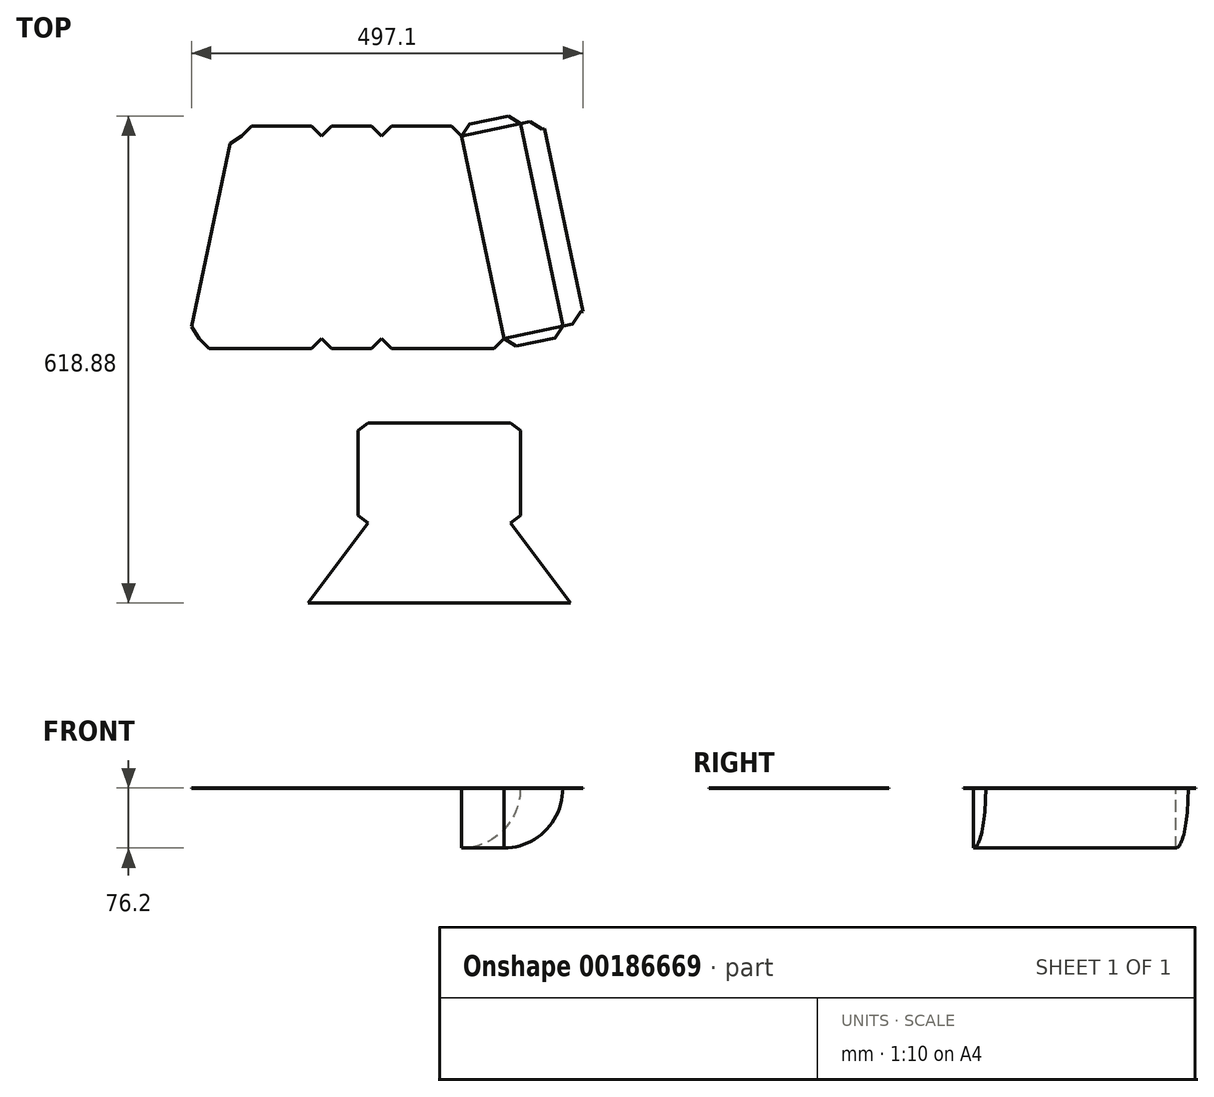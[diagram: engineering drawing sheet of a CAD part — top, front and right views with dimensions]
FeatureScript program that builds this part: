
annotation { "Feature Type Name" : "Feature", "Feature Type Description" : "" }
export const myFeature = defineFeature(function(context is Context, id is Id, definition is map)
    precondition{}
    {
        {
            assignVariable(context, id + "F0", {"name" : "Length", "anyValue" : 10.12});
        }
        {
            var Q0;
            Q0=qCreatedBy(makeId("Front.planeOp"),FACE);
            var sketch = newSketch(context, id + "F1", { "sketchPlane" : qUnion([Q0])});
            skLineSegment(sketch, "E0.bottom", {"start": v(-75.35, 24.33) * mm, "end": v(80.22, 24.33) * mm});
            skLineSegment(sketch, "E0.top", {"start": v(-75.35, -51.87) * mm, "end": v(80.22, -51.87) * mm});
            skLineSegment(sketch, "E0.left", {"start": v(-75.35, 24.33) * mm, "end": v(-75.35, -51.87) * mm});
            skLineSegment(sketch, "E0.right", {"start": v(80.22, 24.33) * mm, "end": v(80.22, -51.87) * mm});
            skSolve(sketch);
        }
        {
            var Q0;
            Q0=qCreatedBy(makeId("Front.planeOp"),FACE);
            cPlane(context, id + "F2", {"entities" : qUnion([Q0]), "cplaneType" : CPlaneType.OFFSET, "offset" : (getVariable(context, 'Length')) * mm, "oppositeDirection" : true, "width" : 152.4 * mm, "height" : 152.4 * mm});
        }
        {
            var Q0;
            Q0=qCreatedBy(id+"F2.planeOp",FACE);
            var sketch = newSketch(context, id + "F3", { "sketchPlane" : qUnion([Q0])});
            skLineSegment(sketch, "E1.bottom", {"start": v(-75.35, 24.33) * mm, "end": v(26.25, 24.33) * mm});
            skLineSegment(sketch, "E1.top", {"start": v(-75.35, -51.87) * mm, "end": v(26.25, -51.87) * mm});
            skLineSegment(sketch, "E1.left", {"start": v(-75.35, 24.33) * mm, "end": v(-75.35, -51.87) * mm});
            skLineSegment(sketch, "E1.right", {"start": v(26.25, 24.33) * mm, "end": v(26.25, -51.87) * mm});
            skSolve(sketch);
        }
        {
            var Q0;
            Q0=sQuery(id+"F3.wireOp",EDGE,"E1.bottom");
            var Q1;
            Q1=sQuery(id+"F1.wireOp",EDGE,"E0.bottom");
            cPlane(context, id + "F4", {"entities" : qUnion([Q0, Q1]), "cplaneType" : CPlaneType.LINE_ANGLE, "offset" : 25.4 * mm, "angle" : 0 * degree, "width" : 152.4 * mm, "height" : 152.4 * mm});
        }
        {
            var Q0;
            Q0=sQuery(id+"F3.wireOp",EDGE,"E1.top");
            var Q1;
            Q1=sQuery(id+"F1.wireOp",EDGE,"E0.top");
            cPlane(context, id + "F5", {"entities" : qUnion([Q0, Q1]), "cplaneType" : CPlaneType.LINE_ANGLE, "offset" : 25.4 * mm, "angle" : 0 * degree, "width" : 152.4 * mm, "height" : 152.4 * mm});
        }
        {
            var Q0;
            Q0=qCreatedBy(id+"F5.planeOp",FACE);
            var sketch = newSketch(context, id + "F6", { "sketchPlane" : qUnion([Q0])});
            skLineSegment(sketch, "E2", {"start": v(-75.35, -257.18) * mm, "end": v(-75.35, 0) * mm});
            skLineSegment(sketch, "E3", {"start": v(-75.35, 0) * mm, "end": v(80.22, 0) * mm});
            skLineSegment(sketch, "E4", {"start": v(80.22, 0) * mm, "end": v(26.25, -257.18) * mm});
            skLineSegment(sketch, "E5", {"start": v(26.25, -257.18) * mm, "end": v(-75.35, -257.18) * mm});
            skSolve(sketch);
        }
        {
            var Q0;
            Q0=qCreatedBy(id+"F4.planeOp",FACE);
            var sketch = newSketch(context, id + "F7", { "sketchPlane" : qUnion([Q0])});
            skLineSegment(sketch, "E6", {"start": v(-75.35, -257.18) * mm, "end": v(-75.35, 0) * mm});
            skLineSegment(sketch, "E7", {"start": v(-75.35, 0) * mm, "end": v(80.22, 0) * mm});
            skLineSegment(sketch, "E8", {"start": v(80.22, 0) * mm, "end": v(26.25, -257.18) * mm});
            skLineSegment(sketch, "E9", {"start": v(26.25, -257.18) * mm, "end": v(-75.35, -257.18) * mm});
            skSolve(sketch);
        }
        {
            var Q0;
            Q0=sQuery(id+"F7.wireOp",EDGE,"E8");
            var Q1;
            Q1=sQuery(id+"F6.wireOp",EDGE,"E4");
            cPlane(context, id + "F8", {"entities" : qUnion([Q0, Q1]), "cplaneType" : CPlaneType.LINE_ANGLE, "offset" : 25.4 * mm, "angle" : 0 * degree, "width" : 152.4 * mm, "height" : 152.4 * mm});
        }
        {
            var Q0;
            Q0=qCreatedBy(id+"F8.planeOp",FACE);
            var sketch = newSketch(context, id + "F9", { "sketchPlane" : qUnion([Q0])});
            skLineSegment(sketch, "E10", {"start": v(16.48, 24.33) * mm, "end": v(16.48, -51.87) * mm});
            skLineSegment(sketch, "E11", {"start": v(16.48, -51.87) * mm, "end": v(-246.3, -51.87) * mm});
            skLineSegment(sketch, "E12", {"start": v(-246.3, -51.87) * mm, "end": v(-246.3, 24.33) * mm});
            skLineSegment(sketch, "E13", {"start": v(-246.3, 24.33) * mm, "end": v(16.48, 24.33) * mm});
            skSolve(sketch);
        }
        {
            var Q0;
            Q0 = qSketchRegion(id + "F9", true);
            var Q1;
            Q1=sQuery(id+"F7.wireOp",EDGE,"E8");
            revolve(context, id + "F10", {"entities" : qUnion([Q0]), "axis" : qUnion([Q1]), "revolveType" : RevolveType.ONE_DIRECTION, "oppositeDirection" : true, "angle" : 90 * degree});
        }
        {
            var Q0;
            Q0=qCreatedBy(id+"F4.planeOp",FACE);
            var sketch = newSketch(context, id + "F11", { "sketchPlane" : qUnion([Q0])});
            skLineSegment(sketch, "E14", {"start": v(26.25, -257.18) * mm, "end": v(100.82, -272.83) * mm});
            skLineSegment(sketch, "E15", {"start": v(100.82, -272.83) * mm, "end": v(154.8, -15.65) * mm});
            skLineSegment(sketch, "E16", {"start": v(154.8, -15.65) * mm, "end": v(80.22, 0) * mm});
            skLineSegment(sketch, "E17", {"start": v(80.22, 0) * mm, "end": v(26.25, -257.18) * mm});
            skLineSegment(sketch, "E18", {"start": v(-75.35, -257.18) * mm, "end": v(-151.55, -257.18) * mm});
            skLineSegment(sketch, "E19", {"start": v(-151.55, -257.18) * mm, "end": v(-151.55, 0) * mm});
            skLineSegment(sketch, "E20", {"start": v(-151.55, 0) * mm, "end": v(-75.35, 0) * mm});
            skLineSegment(sketch, "E21", {"start": v(-75.35, 0) * mm, "end": v(-75.35, -257.18) * mm});
            skLineSegment(sketch, "E22", {"start": v(-151.55, 0) * mm, "end": v(-307.13, 0) * mm});
            skLineSegment(sketch, "E23", {"start": v(-307.13, 0) * mm, "end": v(-253.15, -257.18) * mm});
            skLineSegment(sketch, "E24", {"start": v(-253.15, -257.18) * mm, "end": v(-151.55, -257.18) * mm});
            skLineSegment(sketch, "E25", {"start": v(-75.35, -257.18) * mm, "end": v(26.25, -257.18) * mm});
            skLineSegment(sketch, "E26", {"start": v(-75.35, 0) * mm, "end": v(80.22, 0) * mm});
            skLineSegment(sketch, "E27", {"start": v(-307.13, 0) * mm, "end": v(-316.95, -15.04) * mm});
            skLineSegment(sketch, "E28", {"start": v(-316.95, -15.04) * mm, "end": v(-268.2, -247.35) * mm});
            skLineSegment(sketch, "E29", {"start": v(-268.2, -247.35) * mm, "end": v(-253.15, -257.18) * mm});
            skLineSegment(sketch, "E30", {"start": v(-280.14, -128.59) * mm, "end": v(-292.57, -131.2) * mm, "construction": true});
            skLineSegment(sketch, "E31", {"start": v(-151.55, -257.18) * mm, "end": v(-138.85, -269.88) * mm});
            skLineSegment(sketch, "E32", {"start": v(-138.85, -269.88) * mm, "end": v(-88.05, -269.88) * mm});
            skLineSegment(sketch, "E33", {"start": v(-88.05, -269.88) * mm, "end": v(-75.35, -257.18) * mm});
            skLineSegment(sketch, "E34", {"start": v(-75.35, -257.18) * mm, "end": v(-62.65, -269.88) * mm});
            skLineSegment(sketch, "E35", {"start": v(-62.65, -269.88) * mm, "end": v(13.55, -269.88) * mm});
            skLineSegment(sketch, "E36", {"start": v(13.55, -269.88) * mm, "end": v(26.25, -257.18) * mm});
            skLineSegment(sketch, "E37", {"start": v(-113.45, -257.18) * mm, "end": v(-113.45, -269.88) * mm, "construction": true});
            skLineSegment(sketch, "E38", {"start": v(-24.55, -257.18) * mm, "end": v(-24.55, -269.88) * mm, "construction": true});
            skLineSegment(sketch, "E39", {"start": v(-151.55, 0) * mm, "end": v(-138.85, 12.7) * mm});
            skLineSegment(sketch, "E40", {"start": v(-138.85, 12.7) * mm, "end": v(-88.05, 12.7) * mm});
            skLineSegment(sketch, "E41", {"start": v(-88.05, 12.7) * mm, "end": v(-75.35, 0) * mm});
            skLineSegment(sketch, "E42", {"start": v(-75.35, 0) * mm, "end": v(-62.65, 12.7) * mm});
            skLineSegment(sketch, "E43", {"start": v(-62.65, 12.7) * mm, "end": v(67.52, 12.7) * mm});
            skLineSegment(sketch, "E44", {"start": v(67.52, 12.7) * mm, "end": v(80.22, 0) * mm});
            skLineSegment(sketch, "E45", {"start": v(-151.55, 0) * mm, "end": v(-164.25, 12.7) * mm});
            skLineSegment(sketch, "E46", {"start": v(-164.25, 12.7) * mm, "end": v(-294.43, 12.7) * mm});
            skLineSegment(sketch, "E47", {"start": v(-294.43, 12.7) * mm, "end": v(-307.13, 0) * mm});
            skLineSegment(sketch, "E48", {"start": v(-253.15, -257.18) * mm, "end": v(-240.45, -269.88) * mm});
            skLineSegment(sketch, "E49", {"start": v(-240.45, -269.88) * mm, "end": v(-164.25, -269.88) * mm});
            skLineSegment(sketch, "E50", {"start": v(-164.25, -269.88) * mm, "end": v(-151.55, -257.18) * mm});
            skLineSegment(sketch, "E51", {"start": v(-202.35, -257.18) * mm, "end": v(-202.35, -269.88) * mm, "construction": true});
            skLineSegment(sketch, "E52", {"start": v(-229.34, 0) * mm, "end": v(-229.34, 12.7) * mm, "construction": true});
            skLineSegment(sketch, "E53", {"start": v(-113.45, 0) * mm, "end": v(-113.45, 12.7) * mm, "construction": true});
            skLineSegment(sketch, "E54", {"start": v(2.43, 0) * mm, "end": v(2.43, 12.7) * mm, "construction": true});
            skLineSegment(sketch, "E55", {"start": v(80.22, 0) * mm, "end": v(95.26, 9.82) * mm});
            skLineSegment(sketch, "E56", {"start": v(95.26, 9.82) * mm, "end": v(144.98, -0.61) * mm});
            skLineSegment(sketch, "E57", {"start": v(144.98, -0.61) * mm, "end": v(154.8, -15.65) * mm});
            skLineSegment(sketch, "E58", {"start": v(100.82, -272.83) * mm, "end": v(85.78, -282.65) * mm});
            skLineSegment(sketch, "E59", {"start": v(85.78, -282.65) * mm, "end": v(36.07, -272.21) * mm});
            skLineSegment(sketch, "E60", {"start": v(36.07, -272.21) * mm, "end": v(26.25, -257.18) * mm});
            skLineSegment(sketch, "E61", {"start": v(63.53, -265) * mm, "end": v(60.92, -277.43) * mm, "construction": true});
            skLineSegment(sketch, "E62", {"start": v(117.5, -7.83) * mm, "end": v(120.12, 4.6) * mm, "construction": true});
            skLineSegment(sketch, "E63", {"start": v(154.8, -15.65) * mm, "end": v(167.22, -18.26) * mm});
            skLineSegment(sketch, "E64", {"start": v(167.22, -18.26) * mm, "end": v(113.25, -275.44) * mm});
            skLineSegment(sketch, "E65", {"start": v(113.25, -275.44) * mm, "end": v(100.82, -272.83) * mm});
            skLineSegment(sketch, "E66", {"start": v(127.8, -144.24) * mm, "end": v(140.24, -146.85) * mm, "construction": true});
            skLineSegment(sketch, "E67", {"start": v(140.24, -146.85) * mm, "end": v(152.67, -149.46) * mm, "construction": true});
            skLineSegment(sketch, "E68", {"start": v(167.22, -18.26) * mm, "end": v(177.05, -33.3) * mm});
            skLineSegment(sketch, "E69", {"start": v(177.05, -33.3) * mm, "end": v(128.29, -265.61) * mm});
            skLineSegment(sketch, "E70", {"start": v(128.29, -265.61) * mm, "end": v(113.25, -275.44) * mm});
            skLineSegment(sketch, "E71", {"start": v(177.05, -33.3) * mm, "end": v(180.15, -33.95) * mm});
            skLineSegment(sketch, "E72", {"start": v(180.15, -33.95) * mm, "end": v(131.4, -266.27) * mm});
            skLineSegment(sketch, "E73", {"start": v(131.4, -266.27) * mm, "end": v(128.29, -265.61) * mm});
            skLineSegment(sketch, "E74", {"start": v(152.67, -149.46) * mm, "end": v(155.77, -150.1) * mm, "construction": true});
            skLineSegment(sketch, "E75", {"start": v(-79.74, 247.33) * mm, "end": v(75.84, 247.33) * mm, "construction": true});
            skLineSegment(sketch, "E76", {"start": v(75.84, 247.33) * mm, "end": v(75.84, 323.53) * mm, "construction": true});
            skLineSegment(sketch, "E77", {"start": v(75.84, 323.53) * mm, "end": v(-79.74, 323.53) * mm, "construction": true});
            skLineSegment(sketch, "E78", {"start": v(-79.74, 323.53) * mm, "end": v(-79.74, 247.33) * mm, "construction": true});
            skLineSegment(sketch, "E79.0", {"start": v(-92.44, 234.63) * mm, "end": v(88.54, 234.63) * mm});
            skLineSegment(sketch, "E79.1", {"start": v(-92.44, 336.23) * mm, "end": v(-92.44, 234.63) * mm});
            skLineSegment(sketch, "E79.2", {"start": v(88.54, 336.23) * mm, "end": v(-92.44, 336.23) * mm});
            skLineSegment(sketch, "E79.3", {"start": v(88.54, 234.63) * mm, "end": v(88.54, 336.23) * mm});
            skLineSegment(sketch, "E80", {"start": v(88.54, 336.23) * mm, "end": v(164.74, 336.23) * mm});
            skLineSegment(sketch, "E81", {"start": v(-92.44, 336.23) * mm, "end": v(-168.64, 336.23) * mm});
            skLineSegment(sketch, "E82.top", {"start": v(-92.44, 107.63) * mm, "end": v(88.54, 107.63) * mm});
            skLineSegment(sketch, "E82.left", {"start": v(-92.44, 234.63) * mm, "end": v(-92.44, 107.63) * mm, "construction": true});
            skLineSegment(sketch, "E82.right", {"start": v(88.54, 234.63) * mm, "end": v(88.54, 107.63) * mm, "construction": true});
            skLineSegment(sketch, "E83", {"start": v(101.24, 117.16) * mm, "end": v(101.24, 225.1) * mm});
            skLineSegment(sketch, "E84", {"start": v(-105.14, 117.16) * mm, "end": v(-105.14, 225.1) * mm});
            skLineSegment(sketch, "E85", {"start": v(-168.64, 336.23) * mm, "end": v(-92.44, 234.63) * mm});
            skLineSegment(sketch, "E86", {"start": v(164.74, 336.23) * mm, "end": v(88.54, 234.63) * mm});
            skLineSegment(sketch, "E87", {"start": v(88.54, 234.63) * mm, "end": v(101.24, 225.1) * mm});
            skLineSegment(sketch, "E88", {"start": v(88.54, 107.63) * mm, "end": v(101.24, 117.16) * mm});
            skLineSegment(sketch, "E89", {"start": v(-92.44, 234.63) * mm, "end": v(-105.14, 225.1) * mm});
            skLineSegment(sketch, "E90", {"start": v(-92.44, 107.63) * mm, "end": v(-105.14, 117.16) * mm});
            skSolve(sketch);
        }
        {
            var Q0;
            Q0 = qSketchRegion(id + "F11", true);
            extrude(context, id + "F12", {"entities" : qUnion([Q0]), "depth" : 0.5 * mm});
        }
    });
